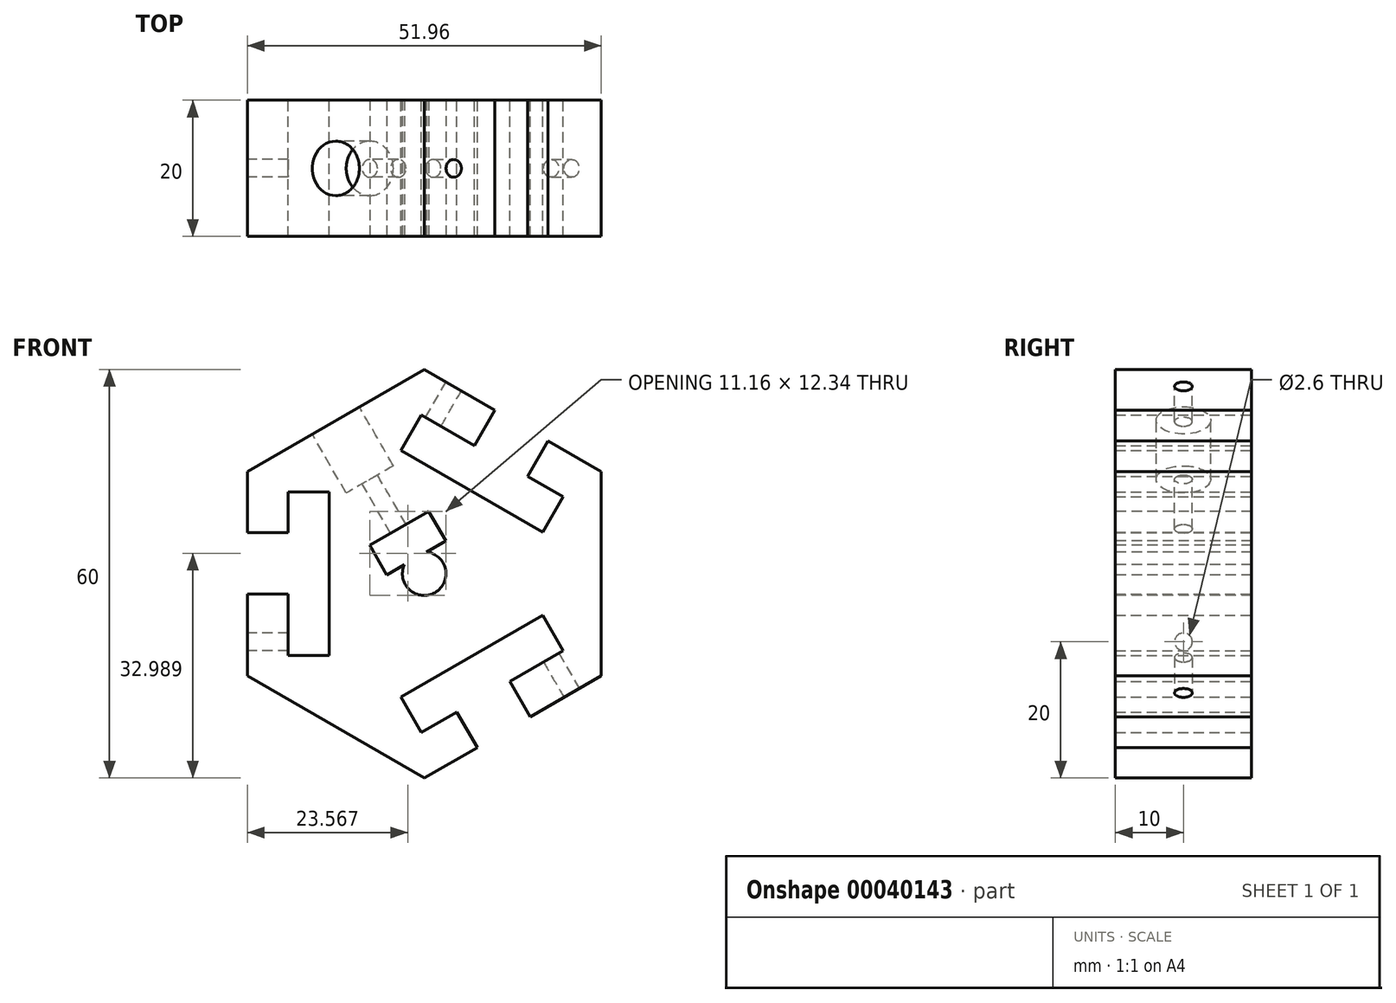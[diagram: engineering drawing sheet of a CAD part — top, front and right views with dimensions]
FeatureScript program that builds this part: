
annotation { "Feature Type Name" : "Feature", "Feature Type Description" : "" }
export const myFeature = defineFeature(function(context is Context, id is Id, definition is map)
    precondition{}
    {
        {
            var Q0;
            Q0=qCreatedBy(makeId("Front.planeOp"),FACE);
            var sketch = newSketch(context, id + "F0", { "sketchPlane" : qUnion([Q0])});
            skCircle(sketch, "E0.cCircle", {"center": v(0, 0) * mm, "radius": 25.98 * mm, "construction": true});
            skLineSegment(sketch, "E0.0", {"start": v(25.98, 15) * mm, "end": v(25.98, -15) * mm});
            skLineSegment(sketch, "E0.2", {"start": v(0, -30) * mm, "end": v(-25.98, -15) * mm});
            skLineSegment(sketch, "E0.3", {"start": v(-25.98, -15) * mm, "end": v(-25.98, -3) * mm});
            skLineSegment(sketch, "E0.4", {"start": v(-25.98, 15) * mm, "end": v(0, 30) * mm});
            skLineSegment(sketch, "E0.5", {"start": v(0, 30) * mm, "end": v(10.4, 24) * mm});
            skPoint(sketch, "E0.0.midPoint", {"position": v(25.98, 0) * mm});
            skLineSegment(sketch, "E1", {"start": v(17.38, 6.1) * mm, "end": v(20.38, 11.3) * mm});
            skLineSegment(sketch, "E2", {"start": v(20.38, 11.3) * mm, "end": v(15.19, 14.3) * mm});
            skLineSegment(sketch, "E3", {"start": v(15.19, 14.3) * mm, "end": v(18.19, 19.5) * mm});
            skLineSegment(sketch, "E4", {"start": v(17.38, 6.1) * mm, "end": v(-3.4, 18.1) * mm});
            skLineSegment(sketch, "E5", {"start": v(-3.4, 18.1) * mm, "end": v(-0.4, 23.3) * mm});
            skLineSegment(sketch, "E6", {"start": v(-0.4, 23.3) * mm, "end": v(7.4, 18.8) * mm});
            skLineSegment(sketch, "E7", {"start": v(7.4, 18.8) * mm, "end": v(10.4, 24) * mm});
            skLineSegment(sketch, "E8.MirrorCS", {"start": v(-13.98, 12) * mm, "end": v(-19.98, 12) * mm});
            skLineSegment(sketch, "E9.MirrorCS", {"start": v(-19.98, -12) * mm, "end": v(-19.98, -3) * mm});
            skLineSegment(sketch, "E10.MirrorCS", {"start": v(-13.98, -12) * mm, "end": v(-19.98, -12) * mm});
            skLineSegment(sketch, "E11.MirrorCS", {"start": v(-19.98, -3) * mm, "end": v(-25.98, -3) * mm});
            skLineSegment(sketch, "E12.MirrorCS", {"start": v(-13.98, 12) * mm, "end": v(-13.98, -12) * mm});
            skLineSegment(sketch, "E13.MirrorCS", {"start": v(-19.98, 12) * mm, "end": v(-19.98, 6) * mm});
            skLineSegment(sketch, "E14.MirrorCS", {"start": v(-19.98, 6) * mm, "end": v(-25.98, 6) * mm});
            skLineSegment(sketch, "E15.trimOffspring", {"start": v(18.19, 19.5) * mm, "end": v(25.98, 15) * mm});
            skLineSegment(sketch, "E16.trimOffspring", {"start": v(-25.98, 6) * mm, "end": v(-25.98, 15) * mm});
            skLineSegment(sketch, "E17", {"start": v(7.8, -25.5) * mm, "end": v(4.8, -20.3) * mm});
            skLineSegment(sketch, "E18", {"start": v(4.8, -20.3) * mm, "end": v(-0.4, -23.3) * mm});
            skLineSegment(sketch, "E19", {"start": v(-0.4, -23.3) * mm, "end": v(-3.4, -18.1) * mm});
            skLineSegment(sketch, "E20", {"start": v(-3.4, -18.1) * mm, "end": v(17.38, -6.1) * mm});
            skLineSegment(sketch, "E21", {"start": v(17.38, -6.1) * mm, "end": v(20.38, -11.3) * mm});
            skLineSegment(sketch, "E22", {"start": v(20.38, -11.3) * mm, "end": v(12.59, -15.8) * mm});
            skLineSegment(sketch, "E23", {"start": v(12.59, -15.8) * mm, "end": v(15.59, -21) * mm});
            skLineSegment(sketch, "E24", {"start": v(15.59, -21) * mm, "end": v(25.98, -15) * mm});
            skLineSegment(sketch, "E25", {"start": v(7.8, -25.5) * mm, "end": v(0, -30) * mm});
            skSolve(sketch);
        }
        {
            var Q0;
            Q0 = qSketchRegion(id + "F0", true);
            extrude(context, id + "F1", {"entities" : qUnion([Q0]), "endBound" : BoundingType.SYMMETRIC, "depth" : 20 * mm});
        }
        {
            var Q0;
            Q0=makeQuery(id+"F1.opExtrude","CAP_FACE",FACE,{"disambiguationData":[OSD([sQuery(id+"F0.wireOp",EDGE,"E0.0"),sQuery(id+"F0.wireOp",EDGE,"E0.1"),sQuery(id+"F0.wireOp",EDGE,"E0.2"),sQuery(id+"F0.wireOp",EDGE,"E0.3"),sQuery(id+"F0.wireOp",EDGE,"E0.4"),sQuery(id+"F0.wireOp",EDGE,"E0.5"),sQuery(id+"F0.wireOp",EDGE,"E1"),sQuery(id+"F0.wireOp",EDGE,"E2"),sQuery(id+"F0.wireOp",EDGE,"E3"),sQuery(id+"F0.wireOp",EDGE,"E4"),sQuery(id+"F0.wireOp",EDGE,"E5"),sQuery(id+"F0.wireOp",EDGE,"E6"),sQuery(id+"F0.wireOp",EDGE,"E7"),sQuery(id+"F0.wireOp",EDGE,"a2ab4075-57fe-42a4-be90-291e31331d100.MirrorCS"),sQuery(id+"F0.wireOp",EDGE,"a2ab4075-57fe-42a4-be90-291e31331d101.MirrorCS"),sQuery(id+"F0.wireOp",EDGE,"a2ab4075-57fe-42a4-be90-291e31331d102.MirrorCS"),sQuery(id+"F0.wireOp",EDGE,"a2ab4075-57fe-42a4-be90-291e31331d103.MirrorCS"),sQuery(id+"F0.wireOp",EDGE,"a2ab4075-57fe-42a4-be90-291e31331d104.MirrorCS"),sQuery(id+"F0.wireOp",EDGE,"a2ab4075-57fe-42a4-be90-291e31331d105.MirrorCS"),sQuery(id+"F0.wireOp",EDGE,"a2ab4075-57fe-42a4-be90-291e31331d106.MirrorCS"),sQuery(id+"F0.wireOp",EDGE,"E8.MirrorCS"),sQuery(id+"F0.wireOp",EDGE,"E9.MirrorCS"),sQuery(id+"F0.wireOp",EDGE,"E10.MirrorCS"),sQuery(id+"F0.wireOp",EDGE,"E11.MirrorCS"),sQuery(id+"F0.wireOp",EDGE,"E12.MirrorCS"),sQuery(id+"F0.wireOp",EDGE,"E13.MirrorCS"),sQuery(id+"F0.wireOp",EDGE,"E14.MirrorCS"),sQuery(id+"F0.wireOp",EDGE,"E15.trimOffspring"),sQuery(id+"F0.wireOp",EDGE,"67ee505a-2bbc-473b-848d-95e59b5eaf8d.trimOffspring"),sQuery(id+"F0.wireOp",EDGE,"E16.trimOffspring")])],"isStart":false});
            var sketch = newSketch(context, id + "F2", { "sketchPlane" : qUnion([Q0])});
            skCircle(sketch, "E26", {"center": v(0, 0) * mm, "radius": 3.2 * mm});
            skLineSegment(sketch, "E27", {"start": v(0.67, 9.16) * mm, "end": v(-8, 4.16) * mm});
            skLineSegment(sketch, "E28", {"start": v(-8, 4.16) * mm, "end": v(-5.5, -0.17) * mm});
            skLineSegment(sketch, "E29", {"start": v(-5.5, -0.17) * mm, "end": v(-2.92, 1.32) * mm});
            skLineSegment(sketch, "E30", {"start": v(0.67, 9.16) * mm, "end": v(3.17, 4.83) * mm});
            skLineSegment(sketch, "E31", {"start": v(3.17, 4.83) * mm, "end": v(0.32, 3.18) * mm});
            skSolve(sketch);
        }
        {
            var Q0;
            Q0 = qSketchRegion(id + "F2", true);
            extrude(context, id + "F3", {"entities" : qUnion([Q0]), "operationType" : NewBodyOperationType.REMOVE, "oppositeDirection" : true, "depth" : 20 * mm});
        }
        {
            var Q0;
            Q0=makeQuery(id+"F1.opExtrude","SWEPT_FACE",FACE,{"disambiguationData":[OSD([sQuery(id+"F0.wireOp",EDGE,"E0.4")])]});
            var sketch = newSketch(context, id + "F4", { "sketchPlane" : qUnion([Q0])});
            skCircle(sketch, "E32", {"center": v(0, 0) * mm, "radius": 4 * mm});
            skCircle(sketch, "E33", {"center": v(0, 0) * mm, "radius": 1.3 * mm});
            skSolve(sketch);
        }
        {
            var Q0;
            Q0=makeQuery(id+"F4.imprint","IMPRINT",FACE,{"disambiguationData":[TD([[makeQuery(id+"F4.imprint","IMPRINT",EDGE,{"derivedFrom":sQuery(id+"F4.wireOp",EDGE,"E33")}),1.0]])]});
            extrude(context, id + "F5", {"entities" : qUnion([Q0]), "operationType" : NewBodyOperationType.REMOVE, "oppositeDirection" : true, "depth" : 25 * mm});
        }
        {
            var Q0;
            Q0 = qSketchRegion(id + "F4", true);
            extrude(context, id + "F6", {"entities" : qUnion([Q0]), "operationType" : NewBodyOperationType.REMOVE, "oppositeDirection" : true, "depth" : 10 * mm});
        }
        {
            var Q0;
            Q0=makeQuery(id+"F1.opExtrude","SWEPT_FACE",FACE,{"disambiguationData":[OSD([sQuery(id+"F0.wireOp",EDGE,"E24")])]});
            var sketch = newSketch(context, id + "F7", { "sketchPlane" : qUnion([Q0])});
            skCircle(sketch, "E34", {"center": v(10, 0) * mm, "radius": 1.3 * mm});
            skSolve(sketch);
        }
        {
            var Q0;
            Q0=makeQuery(id+"F1.opExtrude","SWEPT_FACE",FACE,{"disambiguationData":[OSD([sQuery(id+"F0.wireOp",EDGE,"E0.5")])]});
            var sketch = newSketch(context, id + "F8", { "sketchPlane" : qUnion([Q0])});
            skCircle(sketch, "E35", {"center": v(-10, 0) * mm, "radius": 1.3 * mm});
            skSolve(sketch);
        }
        {
            var Q0;
            Q0 = qSketchRegion(id + "F8", true);
            extrude(context, id + "F9", {"entities" : qUnion([Q0]), "operationType" : NewBodyOperationType.REMOVE, "oppositeDirection" : true, "depth" : 8 * mm});
        }
        {
            var Q0;
            Q0 = qSketchRegion(id + "F7", true);
            extrude(context, id + "F10", {"entities" : qUnion([Q0]), "operationType" : NewBodyOperationType.REMOVE, "oppositeDirection" : true, "depth" : 8 * mm});
        }
        {
            var Q0;
            Q0=makeQuery(id+"F1.opExtrude","SWEPT_FACE",FACE,{"disambiguationData":[OSD([sQuery(id+"F0.wireOp",EDGE,"E0.3")])]});
            var sketch = newSketch(context, id + "F11", { "sketchPlane" : qUnion([Q0])});
            skCircle(sketch, "E36", {"center": v(0, -10) * mm, "radius": 1.3 * mm});
            skSolve(sketch);
        }
        {
            var Q0;
            Q0 = qSketchRegion(id + "F11", true);
            extrude(context, id + "F12", {"entities" : qUnion([Q0]), "operationType" : NewBodyOperationType.REMOVE, "oppositeDirection" : true, "depth" : 8 * mm});
        }
    });
